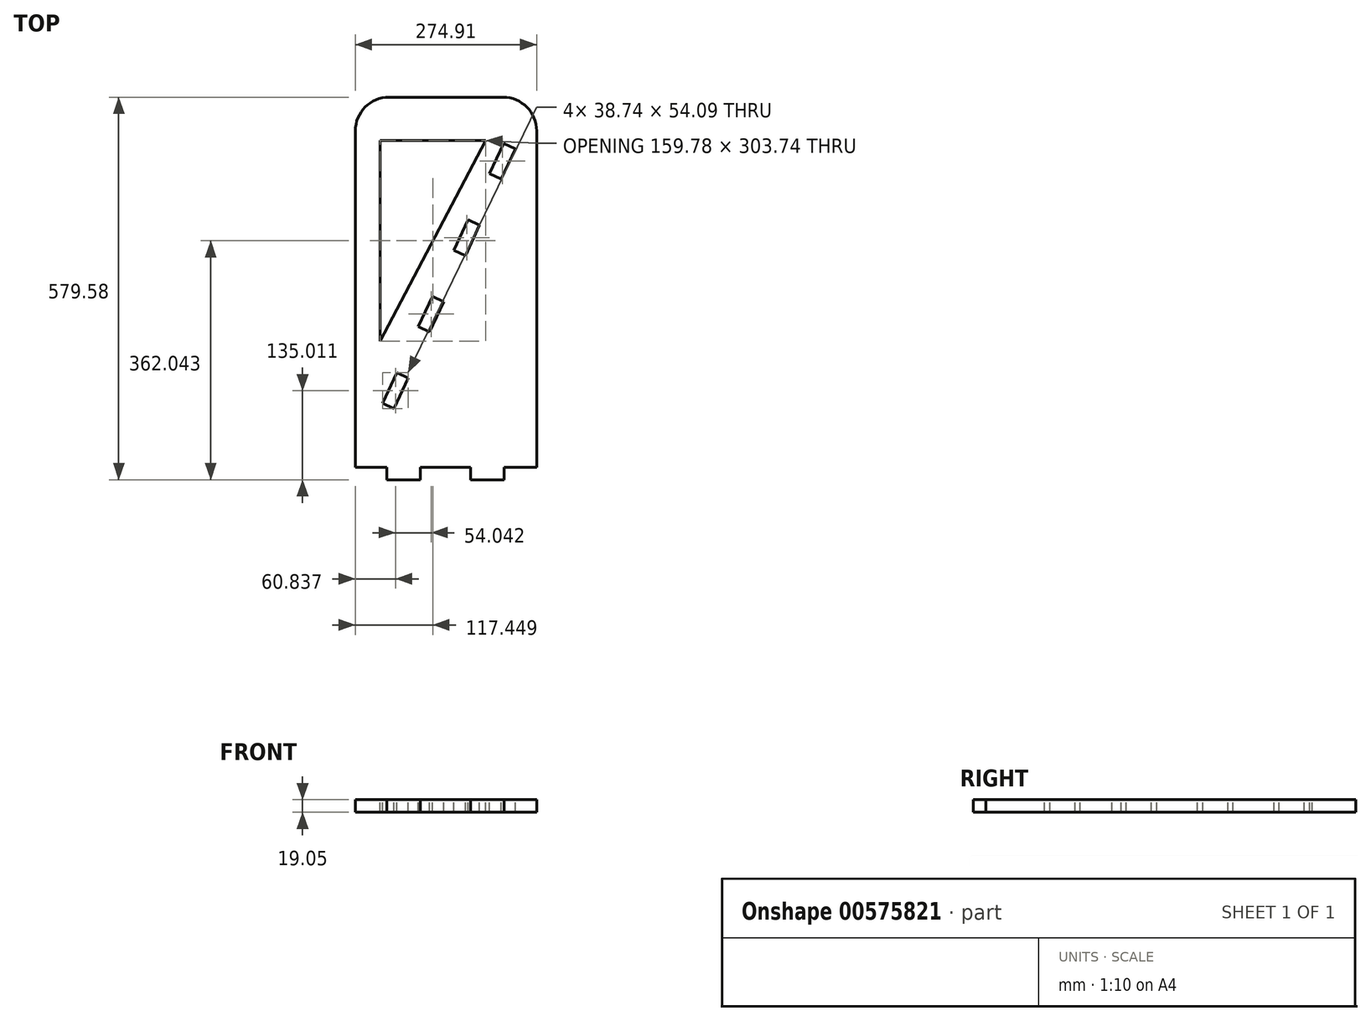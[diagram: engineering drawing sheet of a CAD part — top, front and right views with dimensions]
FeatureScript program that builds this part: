
annotation { "Feature Type Name" : "Feature", "Feature Type Description" : "" }
export const myFeature = defineFeature(function(context is Context, id is Id, definition is map)
    precondition{}
    {
        {
            var Q0;
            Q0=qCreatedBy(makeId("Top.planeOp"),FACE);
            var sketch = newSketch(context, id + "F0", { "sketchPlane" : qUnion([Q0])});
            skLineSegment(sketch, "E0.bottom", {"start": v(-171.13, 297.7) * mm, "end": v(103.78, 297.7) * mm});
            skLineSegment(sketch, "E0.top", {"start": v(-171.13, -262.83) * mm, "end": v(103.78, -262.83) * mm});
            skLineSegment(sketch, "E0.left", {"start": v(-171.13, 297.7) * mm, "end": v(-171.13, -262.83) * mm});
            skLineSegment(sketch, "E0.right", {"start": v(103.78, 297.7) * mm, "end": v(103.78, -262.83) * mm});
            skSolve(sketch);
        }
        {
            var Q0;
            Q0 = qSketchRegion(id + "F0", true);
            extrude(context, id + "F1", {"entities" : qUnion([Q0]), "depth" : 19.05 * mm, "offsetDistance" : 25.4 * mm});
        }
        {
            var Q0;
            Q0=makeQuery(id+"F1.opExtrude","CAP_FACE",FACE,{"disambiguationData":[OSD([sQuery(id+"F0.wireOp",EDGE,"E0.bottom"),sQuery(id+"F0.wireOp",EDGE,"E0.top"),sQuery(id+"F0.wireOp",EDGE,"E0.left"),sQuery(id+"F0.wireOp",EDGE,"E0.right")])],"isStart":false});
            var sketch = newSketch(context, id + "F2", { "sketchPlane" : qUnion([Q0])});
            skLineSegment(sketch, "E1", {"start": v(-153.86, -262.83) * mm, "end": v(103.78, 289.64) * mm});
            skLineSegment(sketch, "E2", {"start": v(-171.13, -254.78) * mm, "end": v(86.5, 297.7) * mm});
            skLineSegment(sketch, "E3", {"start": v(86.5, 297.7) * mm, "end": v(103.78, 289.64) * mm});
            skLineSegment(sketch, "E4", {"start": v(-171.13, -254.78) * mm, "end": v(-153.86, -262.83) * mm});
            skLineSegment(sketch, "E5", {"start": v(53.93, 227.85) * mm, "end": v(71.2, 219.8) * mm});
            skLineSegment(sketch, "E6", {"start": v(71.2, 219.8) * mm, "end": v(49.73, 173.75) * mm});
            skLineSegment(sketch, "E7", {"start": v(49.73, 173.75) * mm, "end": v(32.46, 181.8) * mm});
            skLineSegment(sketch, "E8", {"start": v(32.46, 181.8) * mm, "end": v(53.93, 227.85) * mm});
            skLineSegment(sketch, "E9", {"start": v(17.16, 103.9) * mm, "end": v(-0.1, 111.96) * mm});
            skLineSegment(sketch, "E10", {"start": v(-0.1, 111.96) * mm, "end": v(-21.58, 65.92) * mm});
            skLineSegment(sketch, "E11", {"start": v(-21.58, 65.92) * mm, "end": v(-4.3, 57.86) * mm});
            skLineSegment(sketch, "E12", {"start": v(-4.3, 57.86) * mm, "end": v(17.16, 103.9) * mm});
            skLineSegment(sketch, "E13", {"start": v(-54.15, -3.93) * mm, "end": v(-36.88, -11.99) * mm});
            skLineSegment(sketch, "E14", {"start": v(-36.88, -11.99) * mm, "end": v(-58.35, -58.03) * mm});
            skLineSegment(sketch, "E15", {"start": v(-58.35, -58.03) * mm, "end": v(-75.62, -49.97) * mm});
            skLineSegment(sketch, "E16", {"start": v(-75.62, -49.97) * mm, "end": v(-54.15, -3.93) * mm});
            skLineSegment(sketch, "E17", {"start": v(-108.2, -119.82) * mm, "end": v(-90.92, -127.88) * mm});
            skLineSegment(sketch, "E18", {"start": v(-90.92, -127.88) * mm, "end": v(-112.4, -173.92) * mm});
            skLineSegment(sketch, "E19", {"start": v(-112.4, -173.92) * mm, "end": v(-129.66, -165.86) * mm});
            skLineSegment(sketch, "E20", {"start": v(-129.66, -165.86) * mm, "end": v(-108.2, -119.82) * mm});
            skSolve(sketch);
        }
        {
            var Q0;
            Q0=makeQuery(id+"F2.imprint","IMPRINT",FACE,{"disambiguationData":[TD([[makeQuery(id+"F2.imprint","IMPRINT",EDGE,{"derivedFrom":sQuery(id+"F2.wireOp",EDGE,"E5")}),-1.0]])]});
            var Q1;
            Q1=makeQuery(id+"F2.imprint","IMPRINT",FACE,{"disambiguationData":[TD([[makeQuery(id+"F2.imprint","IMPRINT",EDGE,{"derivedFrom":sQuery(id+"F2.wireOp",EDGE,"E9")}),1.0]])]});
            var Q2;
            Q2=makeQuery(id+"F2.imprint","IMPRINT",FACE,{"disambiguationData":[TD([[makeQuery(id+"F2.imprint","IMPRINT",EDGE,{"derivedFrom":sQuery(id+"F2.wireOp",EDGE,"E13")}),-1.0]])]});
            var Q3;
            Q3=makeQuery(id+"F2.imprint","IMPRINT",FACE,{"disambiguationData":[TD([[makeQuery(id+"F2.imprint","IMPRINT",EDGE,{"derivedFrom":sQuery(id+"F2.wireOp",EDGE,"E17")}),-1.0]])]});
            extrude(context, id + "F3", {"entities" : qUnion([Q0, Q1, Q2, Q3]), "operationType" : NewBodyOperationType.REMOVE, "oppositeDirection" : true, "depth" : 25.4 * mm, "offsetDistance" : 25.4 * mm});
        }
        {
            var Q0;
            Q0=makeQuery(id+"F1.opExtrude","SWEPT_FACE",FACE,{"disambiguationData":[OSD([sQuery(id+"F0.wireOp",EDGE,"E0.top")])]});
            var sketch = newSketch(context, id + "F4", { "sketchPlane" : qUnion([Q0])});
            skLineSegment(sketch, "E21.bottom", {"start": v(-123.2, 19.05) * mm, "end": v(-72.4, 19.05) * mm});
            skLineSegment(sketch, "E21.top", {"start": v(-123.2, 0) * mm, "end": v(-72.4, 0) * mm});
            skLineSegment(sketch, "E21.left", {"start": v(-123.2, 19.05) * mm, "end": v(-123.2, 0) * mm});
            skLineSegment(sketch, "E21.right", {"start": v(-72.4, 19.05) * mm, "end": v(-72.4, 0) * mm});
            skLineSegment(sketch, "E22.bottom", {"start": v(3.8, 19.05) * mm, "end": v(54.6, 19.05) * mm});
            skLineSegment(sketch, "E22.top", {"start": v(3.8, 0) * mm, "end": v(54.6, 0) * mm});
            skLineSegment(sketch, "E22.left", {"start": v(3.8, 19.05) * mm, "end": v(3.8, 0) * mm});
            skLineSegment(sketch, "E22.right", {"start": v(54.6, 19.05) * mm, "end": v(54.6, 0) * mm});
            skSolve(sketch);
        }
        {
            var Q0;
            Q0 = qSketchRegion(id + "F4", true);
            extrude(context, id + "F5", {"entities" : qUnion([Q0]), "operationType" : NewBodyOperationType.ADD, "depth" : 19.05 * mm, "offsetDistance" : 25.4 * mm});
        }
        {
            var Q0;
            Q0=makeQuery(id+"F5.boolean.opBoolean","MERGE",FACE,{"derivedFrom":[makeQuery(id+"F1.opExtrude","CAP_FACE",FACE,{"disambiguationData":[OSD([sQuery(id+"F0.wireOp",EDGE,"E0.bottom"),sQuery(id+"F0.wireOp",EDGE,"E0.top"),sQuery(id+"F0.wireOp",EDGE,"E0.left"),sQuery(id+"F0.wireOp",EDGE,"E0.right")])],"isStart":false}),makeQuery(id+"F5.opExtrude","SWEPT_FACE",FACE,{"disambiguationData":[OSD([sQuery(id+"F4.wireOp",EDGE,"E21.bottom")])]}),makeQuery(id+"F5.opExtrude","SWEPT_FACE",FACE,{"disambiguationData":[OSD([sQuery(id+"F4.wireOp",EDGE,"E22.bottom")])]})]});
            var sketch = newSketch(context, id + "F6", { "sketchPlane" : qUnion([Q0])});
            skLineSegment(sketch, "E23", {"start": v(26.2, 232.03) * mm, "end": v(-133.57, 232.03) * mm});
            skLineSegment(sketch, "E24", {"start": v(-133.57, 232.03) * mm, "end": v(-133.57, -71.7) * mm});
            skLineSegment(sketch, "E25", {"start": v(-133.57, -71.7) * mm, "end": v(26.2, 232.03) * mm});
            skSolve(sketch);
        }
        {
            var Q0;
            Q0 = qSketchRegion(id + "F6", true);
            extrude(context, id + "F7", {"entities" : qUnion([Q0]), "operationType" : NewBodyOperationType.REMOVE, "oppositeDirection" : true, "depth" : 19.05 * mm, "offsetDistance" : 25.4 * mm});
        }
        {
            var Q0;
            Q0=makeQuery(id+"F1.opExtrude","SWEPT_EDGE",EDGE,{"disambiguationData":[OSD([sQuery(id+"F0.wireOp",EDGE,"E0.bottom"),sQuery(id+"F0.wireOp",EDGE,"E0.left")])]});
            var Q1;
            Q1=makeQuery(id+"F1.opExtrude","SWEPT_EDGE",EDGE,{"disambiguationData":[OSD([sQuery(id+"F0.wireOp",EDGE,"E0.bottom"),sQuery(id+"F0.wireOp",EDGE,"E0.right")])]});
            fillet(context, id + "F8", {"entities" : qUnion([Q0, Q1]), "radius" : 50.8 * mm, "tangentPropagation" : true, "allowEdgeOverflow" : false});
        }
    });
